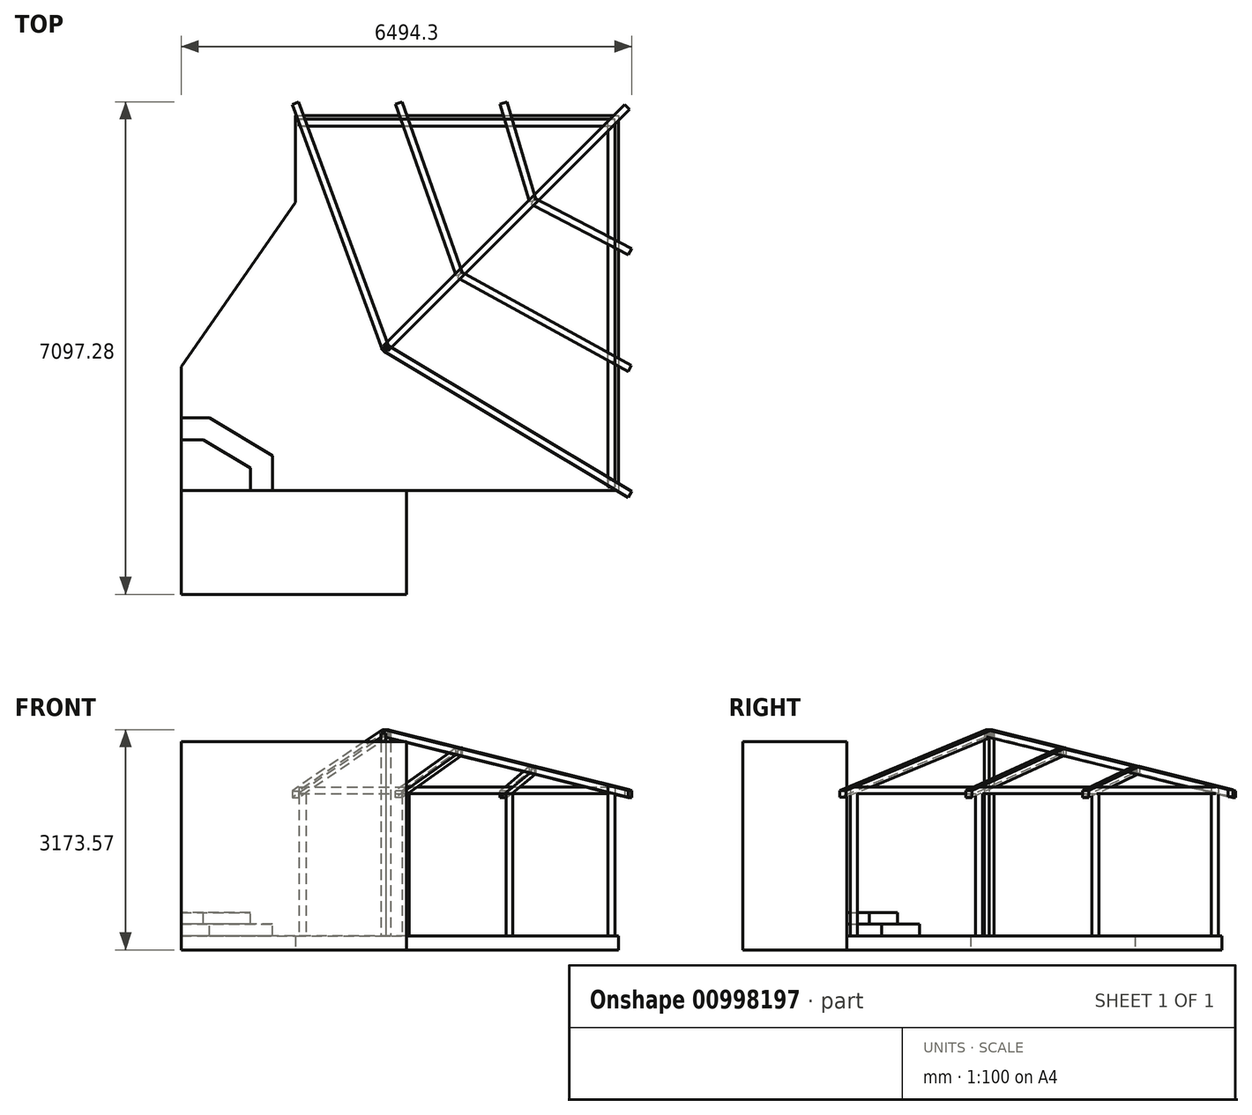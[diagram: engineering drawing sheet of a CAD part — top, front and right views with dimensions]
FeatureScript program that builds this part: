
annotation { "Feature Type Name" : "Feature", "Feature Type Description" : "" }
export const myFeature = defineFeature(function(context is Context, id is Id, definition is map)
    precondition{}
    {
        {
            var Q0;
            Q0=qCreatedBy(makeId("Top.planeOp"),FACE);
            var sketch = newSketch(context, id + "F0", { "sketchPlane" : qUnion([Q0])});
            skLineSegment(sketch, "E0", {"start": v(0, 0) * mm, "end": v(0, -5400) * mm});
            skLineSegment(sketch, "E1", {"start": v(0, -5400) * mm, "end": v(-6300, -5400) * mm});
            skLineSegment(sketch, "E2", {"start": v(-6300, -5400) * mm, "end": v(-6300, -3620) * mm});
            skLineSegment(sketch, "E3", {"start": v(-6300, -3620) * mm, "end": v(-4650, -1250) * mm});
            skLineSegment(sketch, "E4", {"start": v(-4650, -1250) * mm, "end": v(-4650, 0) * mm});
            skLineSegment(sketch, "E5", {"start": v(-4650, 0) * mm, "end": v(0, 0) * mm});
            skSolve(sketch);
        }
        {
            var Q0;
            Q0=makeQuery(id+"F0.imprint","IMPRINT",FACE,{"disambiguationData":[TD([[makeQuery(id+"F0.imprint","IMPRINT",EDGE,{"derivedFrom":sQuery(id+"F0.wireOp",EDGE,"E0")}),-1.0]])]});
            extrude(context, id + "F1", {"entities" : qUnion([Q0]), "depth" : 200 * mm, "offsetDistance" : 25 * mm});
        }
        {
            var Q0;
            Q0=makeQuery(id+"F1.opExtrude","CAP_FACE",FACE,{"disambiguationData":[OSD([sQuery(id+"F0.wireOp",EDGE,"E0"),sQuery(id+"F0.wireOp",EDGE,"E1"),sQuery(id+"F0.wireOp",EDGE,"E2"),sQuery(id+"F0.wireOp",EDGE,"E3"),sQuery(id+"F0.wireOp",EDGE,"E4"),sQuery(id+"F0.wireOp",EDGE,"E5")])],"isStart":false});
            var sketch = newSketch(context, id + "F2", { "sketchPlane" : qUnion([Q0])});
            skLineSegment(sketch, "E6.bottom", {"start": v(-50, -150) * mm, "end": v(-150, -150) * mm});
            skLineSegment(sketch, "E6.top", {"start": v(-50, -50) * mm, "end": v(-150, -50) * mm});
            skLineSegment(sketch, "E6.left", {"start": v(-50, -150) * mm, "end": v(-50, -50) * mm});
            skLineSegment(sketch, "E6.right", {"start": v(-150, -150) * mm, "end": v(-150, -50) * mm});
            skPoint(sketch, "E6.middle", {"position": v(-100, -100) * mm});
            skLineSegment(sketch, "E7", {"start": v(-100, -100) * mm, "end": v(-100, -5400) * mm, "construction": true});
            skLineSegment(sketch, "E8", {"start": v(-100, -100) * mm, "end": v(-4650, -100) * mm, "construction": true});
            skLineSegment(sketch, "E9.bottom", {"start": v(-150, -1870) * mm, "end": v(-50, -1870) * mm});
            skLineSegment(sketch, "E9.top", {"start": v(-150, -1770) * mm, "end": v(-50, -1770) * mm});
            skLineSegment(sketch, "E9.left", {"start": v(-150, -1870) * mm, "end": v(-150, -1770) * mm});
            skLineSegment(sketch, "E9.right", {"start": v(-50, -1870) * mm, "end": v(-50, -1770) * mm});
            skPoint(sketch, "E9.middle", {"position": v(-100, -1820) * mm});
            skLineSegment(sketch, "E10.bottom", {"start": v(-50, -3550) * mm, "end": v(-150, -3550) * mm});
            skLineSegment(sketch, "E10.top", {"start": v(-50, -3450) * mm, "end": v(-150, -3450) * mm});
            skLineSegment(sketch, "E10.left", {"start": v(-50, -3550) * mm, "end": v(-50, -3450) * mm});
            skLineSegment(sketch, "E10.right", {"start": v(-150, -3550) * mm, "end": v(-150, -3450) * mm});
            skPoint(sketch, "E10.middle", {"position": v(-100, -3500) * mm});
            skLineSegment(sketch, "E11.bottom", {"start": v(-1520, -150) * mm, "end": v(-1620, -150) * mm});
            skLineSegment(sketch, "E11.top", {"start": v(-1520, -50) * mm, "end": v(-1620, -50) * mm});
            skLineSegment(sketch, "E11.left", {"start": v(-1520, -150) * mm, "end": v(-1520, -50) * mm});
            skLineSegment(sketch, "E11.right", {"start": v(-1620, -150) * mm, "end": v(-1620, -50) * mm});
            skPoint(sketch, "E11.middle", {"position": v(-1570, -100) * mm});
            skPoint(sketch, "E12.middle", {"position": v(-3065, -100) * mm});
            skLineSegment(sketch, "E13.bottom", {"start": v(-4500, -150) * mm, "end": v(-4600, -150) * mm});
            skLineSegment(sketch, "E13.top", {"start": v(-4500, -50) * mm, "end": v(-4600, -50) * mm});
            skLineSegment(sketch, "E13.left", {"start": v(-4500, -150) * mm, "end": v(-4500, -50) * mm});
            skLineSegment(sketch, "E13.right", {"start": v(-4600, -150) * mm, "end": v(-4600, -50) * mm});
            skPoint(sketch, "E13.middle", {"position": v(-4550, -100) * mm});
            skLineSegment(sketch, "E14.bottom", {"start": v(-3015, -50) * mm, "end": v(-3115, -50) * mm});
            skLineSegment(sketch, "E14.top", {"start": v(-3015, -150) * mm, "end": v(-3115, -150) * mm});
            skLineSegment(sketch, "E14.left", {"start": v(-3015, -50) * mm, "end": v(-3015, -150) * mm});
            skLineSegment(sketch, "E14.right", {"start": v(-3115, -50) * mm, "end": v(-3115, -150) * mm});
            skSolve(sketch);
        }
        {
            var Q0;
            Q0 = qSketchRegion(id + "F2", true);
            extrude(context, id + "F3", {"entities" : qUnion([Q0]), "depth" : 2050 * mm, "offsetDistance" : 25 * mm});
        }
        {
            var Q0;
            Q0=makeQuery(id+"F3.opExtrude","CAP_FACE",FACE,{"disambiguationData":[OSD([sQuery(id+"F2.wireOp",EDGE,"E10.bottom"),sQuery(id+"F2.wireOp",EDGE,"E10.top"),sQuery(id+"F2.wireOp",EDGE,"E10.left"),sQuery(id+"F2.wireOp",EDGE,"E10.right")])],"isStart":false});
            var sketch = newSketch(context, id + "F4", { "sketchPlane" : qUnion([Q0])});
            skPoint(sketch, "E15.0", {"position": v(-4600, -50) * mm});
            skLineSegment(sketch, "E16.bottom", {"start": v(-4600, -50) * mm, "end": v(-50, -50) * mm});
            skLineSegment(sketch, "E16.top", {"start": v(-4600, -150) * mm, "end": v(-150, -150) * mm});
            skLineSegment(sketch, "E16.left", {"start": v(-4600, -50) * mm, "end": v(-4600, -150) * mm});
            skLineSegment(sketch, "E16.right", {"start": v(-50, -50) * mm, "end": v(-50, -150) * mm});
            skPoint(sketch, "E17.0", {"position": v(-150, -3550) * mm});
            skLineSegment(sketch, "E18.bottom", {"start": v(-50, -50) * mm, "end": v(-150, -50) * mm});
            skLineSegment(sketch, "E18.top", {"start": v(-50, -3550) * mm, "end": v(-150, -3550) * mm});
            skLineSegment(sketch, "E18.left", {"start": v(-50, -50) * mm, "end": v(-50, -3550) * mm});
            skLineSegment(sketch, "E18.right", {"start": v(-150, -150) * mm, "end": v(-150, -3550) * mm});
            skLineSegment(sketch, "E19", {"start": v(-150, -150) * mm, "end": v(-50, -50) * mm});
            skSolve(sketch);
        }
        {
            var Q0;
            Q0 = qSketchRegion(id + "F4", true);
            extrude(context, id + "F5", {"entities" : qUnion([Q0]), "depth" : 100 * mm, "offsetDistance" : 25 * mm});
        }
        {
            var Q0;
            Q0=qCreatedBy(makeId("Top.planeOp"),FACE);
            var sketch = newSketch(context, id + "F6", { "sketchPlane" : qUnion([Q0])});
            skPoint(sketch, "E20.0", {"position": v(-6300, -5400) * mm});
            skLineSegment(sketch, "E21.bottom", {"start": v(-6300, -5400) * mm, "end": v(-3050, -5400) * mm});
            skLineSegment(sketch, "E21.top", {"start": v(-6300, -6900) * mm, "end": v(-3050, -6900) * mm});
            skLineSegment(sketch, "E21.left", {"start": v(-6300, -5400) * mm, "end": v(-6300, -6900) * mm});
            skLineSegment(sketch, "E21.right", {"start": v(-3050, -5400) * mm, "end": v(-3050, -6900) * mm});
            skSolve(sketch);
        }
        {
            var Q0;
            Q0=makeQuery(id+"F5.opExtrude","SWEPT_FACE",FACE,{"disambiguationData":[OSD([sQuery(id+"F4.wireOp",EDGE,"E18.right")])]});
            var Q1;
            Q1=makeQuery(id+"F5.opExtrude","SWEPT_FACE",FACE,{"disambiguationData":[OSD([sQuery(id+"F4.wireOp",EDGE,"E16.top")])]});
            cPlane(context, id + "F7", {"entities" : qUnion([Q0, Q1]), "cplaneType" : CPlaneType.MID_PLANE, "offset" : 25 * mm, "width" : 150 * mm, "height" : 150 * mm});
        }
        {
            var Q0;
            Q0=makeQuery(id+"F1.opExtrude","CAP_FACE",FACE,{"disambiguationData":[OSD([sQuery(id+"F0.wireOp",EDGE,"E0"),sQuery(id+"F0.wireOp",EDGE,"E1"),sQuery(id+"F0.wireOp",EDGE,"E2"),sQuery(id+"F0.wireOp",EDGE,"E3"),sQuery(id+"F0.wireOp",EDGE,"E4"),sQuery(id+"F0.wireOp",EDGE,"E5")])],"isStart":false});
            var sketch = newSketch(context, id + "F8", { "sketchPlane" : qUnion([Q0])});
            skLineSegment(sketch, "E22.0", {"start": v(-100, -100) * mm, "end": v(-100, -5400) * mm, "construction": true});
            skLineSegment(sketch, "E23.bottom", {"start": v(-150, -5250) * mm, "end": v(-50, -5250) * mm});
            skLineSegment(sketch, "E23.top", {"start": v(-150, -5350) * mm, "end": v(-50, -5350) * mm});
            skLineSegment(sketch, "E23.left", {"start": v(-150, -5250) * mm, "end": v(-150, -5350) * mm});
            skLineSegment(sketch, "E23.right", {"start": v(-50, -5250) * mm, "end": v(-50, -5350) * mm});
            skPoint(sketch, "E23.middle", {"position": v(-100, -5300) * mm});
            skSolve(sketch);
        }
        {
            var Q0;
            Q0 = qSketchRegion(id + "F8", true);
            extrude(context, id + "F9", {"entities" : qUnion([Q0]), "operationType" : NewBodyOperationType.ADD, "depth" : 2050 * mm, "offsetDistance" : 25 * mm});
        }
        {
            var Q0;
            Q0=makeQuery(id+"F5.opExtrude","SWEPT_FACE",FACE,{"disambiguationData":[OSD([sQuery(id+"F4.wireOp",EDGE,"E18.top")])]});
            var Q1;
            Q1=makeQuery(id+"F9.opExtrude","SWEPT_FACE",FACE,{"disambiguationData":[OSD([sQuery(id+"F8.wireOp",EDGE,"E23.top")])]});
            extrude(context, id + "F10", {"entities" : qUnion([Q0]), "operationType" : NewBodyOperationType.ADD, "endBound" : BoundingType.UP_TO_SURFACE, "depth" : 25 * mm, "endBoundEntityFace" : qUnion([Q1]), "offsetDistance" : 25 * mm});
        }
        {
            var Q0;
            Q0=makeQuery(id+"F8.imprint","IMPRINT",FACE,{"disambiguationData":[TD([[makeQuery(id+"F8.imprint","IMPRINT",EDGE,{"derivedFrom":sQuery(id+"F8.wireOp",EDGE,"E23.bottom")}),1.0]])]});
            var sketch = newSketch(context, id + "F11", { "sketchPlane" : qUnion([Q0])});
            skPoint(sketch, "E24.0", {"position": v(-100, -100) * mm});
            skPoint(sketch, "E25.0", {"position": v(-4550, -100) * mm});
            skPoint(sketch, "E26.0", {"position": v(-100, -5300) * mm});
            skLineSegment(sketch, "E27", {"start": v(-100, -100) * mm, "end": v(-1231.37, -1231.37) * mm, "construction": true});
            skLineSegment(sketch, "E28", {"start": v(-3352.7, -3352.7) * mm, "end": v(-4550, -100) * mm, "construction": true});
            skLineSegment(sketch, "E29", {"start": v(-3352.7, -3352.7) * mm, "end": v(-100, -5300) * mm, "construction": true});
            skPoint(sketch, "E30.0", {"position": v(-100, -1820) * mm});
            skPoint(sketch, "E31.0", {"position": v(-100, -3500) * mm});
            skPoint(sketch, "E32.0", {"position": v(-1570, -100) * mm});
            skPoint(sketch, "E33.0", {"position": v(-3065, -100) * mm});
            skLineSegment(sketch, "E34", {"start": v(-100, -1820) * mm, "end": v(-1231.37, -1231.37) * mm, "construction": true});
            skLineSegment(sketch, "E35", {"start": v(-100, -3500) * mm, "end": v(-2292.03, -2292.03) * mm, "construction": true});
            skLineSegment(sketch, "E36", {"start": v(-1231.37, -1231.37) * mm, "end": v(-1231.37, -1231.37) * mm});
            skLineSegment(sketch, "E37", {"start": v(-2292.03, -2292.03) * mm, "end": v(-3065, -100) * mm, "construction": true});
            skLineSegment(sketch, "E38", {"start": v(-2292.03, -2292.03) * mm, "end": v(-3352.7, -3352.7) * mm, "construction": true});
            skLineSegment(sketch, "E39", {"start": v(-1231.37, -1231.37) * mm, "end": v(-1570, -100) * mm, "construction": true});
            skLineSegment(sketch, "E40", {"start": v(-1231.37, -1231.37) * mm, "end": v(-2292.03, -2292.03) * mm, "construction": true});
            skSolve(sketch);
        }
        {
            var Q0;
            Q0=qCreatedBy(id+"F7.planeOp",FACE);
            var sketch = newSketch(context, id + "F12", { "sketchPlane" : qUnion([Q0])});
            skLineSegment(sketch, "E41", {"start": v(4741.42, 3123.57) * mm, "end": v(-175.5, 2256.59) * mm});
            skPoint(sketch, "E42.0", {"position": v(3818.38, 200) * mm});
            skPoint(sketch, "E43.0", {"position": v(3288.05, 200) * mm});
            skPoint(sketch, "E44.0", {"position": v(4741.42, 200) * mm});
            skLineSegment(sketch, "E45", {"start": v(4741.42, 3123.57) * mm, "end": v(4741.42, 200) * mm, "construction": true});
            skPoint(sketch, "E46.0", {"position": v(3241.42, 200) * mm});
            skPoint(sketch, "E47.0", {"position": v(1741.42, 200) * mm});
            skLineSegment(sketch, "E48", {"start": v(3241.42, 200) * mm, "end": v(3241.42, 2859.08) * mm, "construction": true});
            skLineSegment(sketch, "E49", {"start": v(1741.42, 200) * mm, "end": v(1741.42, 2594.6) * mm, "construction": true});
            skSolve(sketch);
        }
        {
            var Q0;
            Q0=sQuery(id+"F12.wireOp",EDGE,"E45");
            var Q1;
            Q1=qCreatedBy(id+"F7.planeOp",FACE);
            cPlane(context, id + "F13", {"entities" : qUnion([Q0, Q1]), "cplaneType" : CPlaneType.LINE_ANGLE, "offset" : 25 * mm, "angle" : 90 * degree, "width" : 150 * mm, "height" : 150 * mm});
        }
        {
            var Q0;
            Q0=qCreatedBy(id+"F13.planeOp",FACE);
            var sketch = newSketch(context, id + "F14", { "sketchPlane" : qUnion([Q0])});
            skPoint(sketch, "E50.0", {"position": v(0, 3123.57) * mm});
            skLineSegment(sketch, "E51.bottom", {"start": v(-50, 3173.57) * mm, "end": v(50, 3173.57) * mm});
            skLineSegment(sketch, "E51.top", {"start": v(-50, 3073.57) * mm, "end": v(50, 3073.57) * mm});
            skLineSegment(sketch, "E51.left", {"start": v(-50, 3173.57) * mm, "end": v(-50, 3073.57) * mm});
            skLineSegment(sketch, "E51.right", {"start": v(50, 3173.57) * mm, "end": v(50, 3073.57) * mm});
            skSolve(sketch);
        }
        {
            var Q0;
            Q0=makeQuery(id+"F14.imprint","IMPRINT",FACE,{"disambiguationData":[TD([[makeQuery(id+"F14.imprint","IMPRINT",EDGE,{"derivedFrom":sQuery(id+"F14.wireOp",EDGE,"E51.bottom")}),-1.0]])]});
            var Q1;
            Q1=sQuery(id+"F12.wireOp",EDGE,"E41");
            sweep(context, id + "F15", {"profiles" : qUnion([Q0]), "path" : qUnion([Q1])});
        }
        {
            var Q0;
            Q0=sQuery(id+"F12.wireOp",EDGE,"E45");
            var Q1;
            Q1=sQuery(id+"F11.wireOp",EDGE,"E29");
            cPlane(context, id + "F16", {"entities" : qUnion([Q0, Q1]), "cplaneType" : CPlaneType.LINE_ANGLE, "offset" : 25 * mm, "angle" : 0 * degree, "width" : 150 * mm, "height" : 150 * mm});
        }
        {
            var Q0;
            Q0=qCreatedBy(id+"F16.planeOp",FACE);
            var sketch = newSketch(context, id + "F17", { "sketchPlane" : qUnion([Q0])});
            skPoint(sketch, "E52.0", {"position": v(2636.6, 200) * mm});
            skPoint(sketch, "E53.0", {"position": v(2662.28, 2250) * mm});
            skLineSegment(sketch, "E54", {"start": v(2636.6, 200) * mm, "end": v(2636.6, 2250) * mm, "construction": true});
            skPoint(sketch, "E55.0", {"position": v(-1154.44, 3123.57) * mm});
            skPoint(sketch, "E56.0", {"position": v(2705.18, 2300) * mm});
            skLineSegment(sketch, "E57", {"start": v(-1154.44, 3123.57) * mm, "end": v(2949.68, 2247.83) * mm});
            skSolve(sketch);
        }
        {
            var Q0;
            Q0=sQuery(id+"F12.wireOp",EDGE,"E45");
            var Q1;
            Q1=qCreatedBy(id+"F16.planeOp",FACE);
            cPlane(context, id + "F18", {"entities" : qUnion([Q0, Q1]), "cplaneType" : CPlaneType.LINE_ANGLE, "offset" : 25 * mm, "angle" : 90 * degree, "width" : 150 * mm, "height" : 150 * mm});
        }
        {
            var Q0;
            Q0=qCreatedBy(id+"F18.planeOp",FACE);
            var sketch = newSketch(context, id + "F19", { "sketchPlane" : qUnion([Q0])});
            skPoint(sketch, "E58.0", {"position": v(-4598.73, 3123.57) * mm});
            skLineSegment(sketch, "E59.bottom", {"start": v(-4648.73, 3173.57) * mm, "end": v(-4548.73, 3173.57) * mm});
            skLineSegment(sketch, "E59.top", {"start": v(-4648.73, 3073.57) * mm, "end": v(-4548.73, 3073.57) * mm});
            skLineSegment(sketch, "E59.left", {"start": v(-4648.73, 3173.57) * mm, "end": v(-4648.73, 3073.57) * mm});
            skLineSegment(sketch, "E59.right", {"start": v(-4548.73, 3173.57) * mm, "end": v(-4548.73, 3073.57) * mm});
            skSolve(sketch);
        }
        {
            var Q0;
            Q0 = qSketchRegion(id + "F19", true);
            var Q1;
            Q1=sQuery(id+"F17.wireOp",EDGE,"E57");
            sweep(context, id + "F20", {"profiles" : qUnion([Q0]), "path" : qUnion([Q1])});
        }
        {
            var Q0;
            Q0=sQuery(id+"F12.wireOp",EDGE,"E48");
            var Q1;
            Q1=sQuery(id+"F11.wireOp",EDGE,"E35");
            cPlane(context, id + "F21", {"entities" : qUnion([Q0, Q1]), "cplaneType" : CPlaneType.LINE_ANGLE, "offset" : 25 * mm, "angle" : 0 * degree, "width" : 150 * mm, "height" : 150 * mm});
        }
        {
            var Q0;
            Q0=qCreatedBy(id+"F21.planeOp",FACE);
            var sketch = newSketch(context, id + "F22", { "sketchPlane" : qUnion([Q0])});
            skPoint(sketch, "E60.0", {"position": v(-901.18, 2859.08) * mm});
            skLineSegment(sketch, "E61", {"start": v(1658.75, 2350) * mm, "end": v(1658.75, 2250) * mm, "construction": true});
            skPoint(sketch, "E62", {"position": v(1658.75, 2300) * mm});
            skLineSegment(sketch, "E63", {"start": v(-901.18, 2859.08) * mm, "end": v(1903, 2246.66) * mm});
            skSolve(sketch);
        }
        {
            var Q0;
            Q0=sQuery(id+"F12.wireOp",EDGE,"E48");
            var Q1;
            Q1=qCreatedBy(id+"F21.planeOp",FACE);
            cPlane(context, id + "F23", {"entities" : qUnion([Q0, Q1]), "cplaneType" : CPlaneType.LINE_ANGLE, "offset" : 25 * mm, "angle" : 90 * degree, "width" : 150 * mm, "height" : 150 * mm});
        }
        {
            var Q0;
            Q0=qCreatedBy(id+"F23.planeOp",FACE);
            var sketch = newSketch(context, id + "F24", { "sketchPlane" : qUnion([Q0])});
            skPoint(sketch, "E64.0", {"position": v(3113.63, 2859.08) * mm});
            skLineSegment(sketch, "E65.bottom", {"start": v(3063.63, 2909.08) * mm, "end": v(3163.63, 2909.08) * mm});
            skLineSegment(sketch, "E65.top", {"start": v(3063.63, 2809.08) * mm, "end": v(3163.63, 2809.08) * mm});
            skLineSegment(sketch, "E65.left", {"start": v(3063.63, 2909.08) * mm, "end": v(3063.63, 2809.08) * mm});
            skLineSegment(sketch, "E65.right", {"start": v(3163.63, 2909.08) * mm, "end": v(3163.63, 2809.08) * mm});
            skSolve(sketch);
        }
        {
            var Q0;
            Q0 = qSketchRegion(id + "F24", true);
            var Q1;
            Q1=sQuery(id+"F22.wireOp",EDGE,"E63");
            sweep(context, id + "F25", {"profiles" : qUnion([Q0]), "path" : qUnion([Q1])});
        }
        {
            var Q0;
            Q0=sQuery(id+"F12.wireOp",EDGE,"E49");
            var Q1;
            Q1=sQuery(id+"F11.wireOp",EDGE,"E34");
            cPlane(context, id + "F26", {"entities" : qUnion([Q0, Q1]), "cplaneType" : CPlaneType.LINE_ANGLE, "offset" : 25 * mm, "angle" : 0 * degree, "width" : 150 * mm, "height" : 150 * mm});
        }
        {
            var Q0;
            Q0=qCreatedBy(id+"F26.planeOp",FACE);
            var sketch = newSketch(context, id + "F27", { "sketchPlane" : qUnion([Q0])});
            skPoint(sketch, "E66.0", {"position": v(-524.03, 2594.6) * mm});
            skLineSegment(sketch, "E67", {"start": v(807.67, 2350) * mm, "end": v(807.67, 2250) * mm, "construction": true});
            skPoint(sketch, "E68", {"position": v(807.67, 2300) * mm});
            skLineSegment(sketch, "E69", {"start": v(-524.03, 2594.6) * mm, "end": v(1051.77, 2246) * mm});
            skSolve(sketch);
        }
        {
            var Q0;
            Q0=qCreatedBy(id+"F26.planeOp",FACE);
            var Q1;
            Q1=sQuery(id+"F12.wireOp",EDGE,"E49");
            cPlane(context, id + "F28", {"entities" : qUnion([Q0, Q1]), "cplaneType" : CPlaneType.LINE_ANGLE, "offset" : 25 * mm, "angle" : 90 * degree, "width" : 150 * mm, "height" : 150 * mm});
        }
        {
            var Q0;
            Q0=qCreatedBy(id+"F28.planeOp",FACE);
            var sketch = newSketch(context, id + "F29", { "sketchPlane" : qUnion([Q0])});
            skPoint(sketch, "E70.0", {"position": v(1660.7, 2594.6) * mm});
            skLineSegment(sketch, "E71.bottom", {"start": v(1610.7, 2644.6) * mm, "end": v(1710.7, 2644.6) * mm});
            skLineSegment(sketch, "E71.top", {"start": v(1610.7, 2544.6) * mm, "end": v(1710.7, 2544.6) * mm});
            skLineSegment(sketch, "E71.left", {"start": v(1610.7, 2644.6) * mm, "end": v(1610.7, 2544.6) * mm});
            skLineSegment(sketch, "E71.right", {"start": v(1710.7, 2644.6) * mm, "end": v(1710.7, 2544.6) * mm});
            skSolve(sketch);
        }
        {
            var Q0;
            Q0 = qSketchRegion(id + "F29", true);
            var Q1;
            Q1=sQuery(id+"F27.wireOp",EDGE,"E69");
            sweep(context, id + "F30", {"profiles" : qUnion([Q0]), "path" : qUnion([Q1])});
        }
        {
            var Q0;
            Q0=sQuery(id+"F11.wireOp",EDGE,"E39");
            var Q1;
            Q1=sQuery(id+"F12.wireOp",EDGE,"E49");
            cPlane(context, id + "F31", {"entities" : qUnion([Q0, Q1]), "cplaneType" : CPlaneType.LINE_ANGLE, "offset" : 25 * mm, "angle" : 0 * degree, "width" : 150 * mm, "height" : 150 * mm});
        }
        {
            var Q0;
            Q0=qCreatedBy(id+"F31.planeOp",FACE);
            var sketch = newSketch(context, id + "F32", { "sketchPlane" : qUnion([Q0])});
            skPoint(sketch, "E72.0", {"position": v(-826.58, 2594.6) * mm});
            skLineSegment(sketch, "E73", {"start": v(406.57, 2350) * mm, "end": v(406.57, 2250) * mm, "construction": true});
            skPoint(sketch, "E74", {"position": v(406.57, 2300) * mm});
            skLineSegment(sketch, "E75", {"start": v(-826.58, 2594.6) * mm, "end": v(649.73, 2241.91) * mm});
            skSolve(sketch);
        }
        {
            var Q0;
            Q0=qCreatedBy(id+"F31.planeOp",FACE);
            var Q1;
            Q1=sQuery(id+"F12.wireOp",EDGE,"E49");
            cPlane(context, id + "F33", {"entities" : qUnion([Q0, Q1]), "cplaneType" : CPlaneType.LINE_ANGLE, "offset" : 25 * mm, "angle" : 90 * degree, "width" : 150 * mm, "height" : 150 * mm});
        }
        {
            var Q0;
            Q0=qCreatedBy(id+"F33.planeOp",FACE);
            var sketch = newSketch(context, id + "F34", { "sketchPlane" : qUnion([Q0])});
            skPoint(sketch, "E76.0", {"position": v(-1532.75, 2594.6) * mm});
            skLineSegment(sketch, "E77.bottom", {"start": v(-1482.75, 2544.6) * mm, "end": v(-1582.75, 2544.6) * mm});
            skLineSegment(sketch, "E77.top", {"start": v(-1482.75, 2644.6) * mm, "end": v(-1582.75, 2644.6) * mm});
            skLineSegment(sketch, "E77.left", {"start": v(-1482.75, 2544.6) * mm, "end": v(-1482.75, 2644.6) * mm});
            skLineSegment(sketch, "E77.right", {"start": v(-1582.75, 2544.6) * mm, "end": v(-1582.75, 2644.6) * mm});
            skSolve(sketch);
        }
        {
            var Q0;
            Q0 = qSketchRegion(id + "F34", true);
            var Q1;
            Q1=sQuery(id+"F32.wireOp",EDGE,"E75");
            sweep(context, id + "F35", {"profiles" : qUnion([Q0]), "path" : qUnion([Q1])});
        }
        {
            var Q0;
            Q0=sQuery(id+"F12.wireOp",EDGE,"E48");
            var Q1;
            Q1=sQuery(id+"F11.wireOp",EDGE,"E37");
            cPlane(context, id + "F36", {"entities" : qUnion([Q0, Q1]), "cplaneType" : CPlaneType.LINE_ANGLE, "offset" : 25 * mm, "angle" : 0 * degree, "width" : 150 * mm, "height" : 150 * mm});
        }
        {
            var Q0;
            Q0=qCreatedBy(id+"F36.planeOp",FACE);
            var sketch = newSketch(context, id + "F37", { "sketchPlane" : qUnion([Q0])});
            skPoint(sketch, "E78.0", {"position": v(1399.35, 2859.08) * mm});
            skLineSegment(sketch, "E79", {"start": v(-978, 2250) * mm, "end": v(-978, 2350) * mm, "construction": true});
            skPoint(sketch, "E80", {"position": v(-978, 2300) * mm});
            skLineSegment(sketch, "E81", {"start": v(1399.35, 2859.08) * mm, "end": v(-1221.36, 2242.77) * mm});
            skSolve(sketch);
        }
        {
            var Q0;
            Q0=qCreatedBy(id+"F36.planeOp",FACE);
            var Q1;
            Q1=sQuery(id+"F12.wireOp",EDGE,"E48");
            cPlane(context, id + "F38", {"entities" : qUnion([Q0, Q1]), "cplaneType" : CPlaneType.LINE_ANGLE, "offset" : 25 * mm, "angle" : 90 * degree, "width" : 150 * mm, "height" : 150 * mm});
        }
        {
            var Q0;
            Q0=qCreatedBy(id+"F38.planeOp",FACE);
            var sketch = newSketch(context, id + "F39", { "sketchPlane" : qUnion([Q0])});
            skPoint(sketch, "E82.0", {"position": v(2923.8, 2859.08) * mm});
            skLineSegment(sketch, "E83.bottom", {"start": v(2873.8, 2809.08) * mm, "end": v(2973.8, 2809.08) * mm});
            skLineSegment(sketch, "E83.top", {"start": v(2873.8, 2909.08) * mm, "end": v(2973.8, 2909.08) * mm});
            skLineSegment(sketch, "E83.left", {"start": v(2873.8, 2809.08) * mm, "end": v(2873.8, 2909.08) * mm});
            skLineSegment(sketch, "E83.right", {"start": v(2973.8, 2809.08) * mm, "end": v(2973.8, 2909.08) * mm});
            skSolve(sketch);
        }
        {
            var Q0;
            Q0 = qSketchRegion(id + "F39", true);
            var Q1;
            Q1=sQuery(id+"F37.wireOp",EDGE,"E81");
            sweep(context, id + "F40", {"profiles" : qUnion([Q0]), "path" : qUnion([Q1])});
        }
        {
            var Q0;
            Q0=sQuery(id+"F12.wireOp",EDGE,"E45");
            var Q1;
            Q1=sQuery(id+"F11.wireOp",EDGE,"E28");
            cPlane(context, id + "F41", {"entities" : qUnion([Q0, Q1]), "cplaneType" : CPlaneType.LINE_ANGLE, "offset" : 25 * mm, "angle" : 0 * degree, "width" : 150 * mm, "height" : 150 * mm});
        }
        {
            var Q0;
            Q0=qCreatedBy(id+"F41.planeOp",FACE);
            var sketch = newSketch(context, id + "F42", { "sketchPlane" : qUnion([Q0])});
            skPoint(sketch, "E84.0", {"position": v(-1988.16, 3123.57) * mm});
            skLineSegment(sketch, "E85", {"start": v(1531.18, 2350) * mm, "end": v(1531.18, 2250) * mm, "construction": true});
            skPoint(sketch, "E86", {"position": v(1531.18, 2300) * mm});
            skLineSegment(sketch, "E87", {"start": v(-1988.16, 3123.57) * mm, "end": v(1774.6, 2243.04) * mm});
            skSolve(sketch);
        }
        {
            var Q0;
            Q0=qCreatedBy(id+"F41.planeOp",FACE);
            var Q1;
            Q1=sQuery(id+"F12.wireOp",EDGE,"E45");
            cPlane(context, id + "F43", {"entities" : qUnion([Q0, Q1]), "cplaneType" : CPlaneType.LINE_ANGLE, "offset" : 25 * mm, "angle" : 90 * degree, "width" : 150 * mm, "height" : 150 * mm});
        }
        {
            var Q0;
            Q0=qCreatedBy(id+"F43.planeOp",FACE);
            var sketch = newSketch(context, id + "F44", { "sketchPlane" : qUnion([Q0])});
            skPoint(sketch, "E88.0", {"position": v(4304.45, 3123.57) * mm});
            skLineSegment(sketch, "E89.bottom", {"start": v(4354.45, 3173.57) * mm, "end": v(4254.45, 3173.57) * mm});
            skLineSegment(sketch, "E89.top", {"start": v(4354.45, 3073.57) * mm, "end": v(4254.45, 3073.57) * mm});
            skLineSegment(sketch, "E89.left", {"start": v(4354.45, 3173.57) * mm, "end": v(4354.45, 3073.57) * mm});
            skLineSegment(sketch, "E89.right", {"start": v(4254.45, 3173.57) * mm, "end": v(4254.45, 3073.57) * mm});
            skSolve(sketch);
        }
        {
            var Q0;
            Q0 = qSketchRegion(id + "F44", true);
            var Q1;
            Q1=sQuery(id+"F42.wireOp",EDGE,"E87");
            sweep(context, id + "F45", {"profiles" : qUnion([Q0]), "path" : qUnion([Q1])});
        }
        {
            var Q0;
            Q0=makeQuery(id+"F8.imprint","IMPRINT",FACE,{"disambiguationData":[TD([[makeQuery(id+"F8.imprint","IMPRINT",EDGE,{"derivedFrom":sQuery(id+"F8.wireOp",EDGE,"E23.bottom")}),1.0]])]});
            var sketch = newSketch(context, id + "F46", { "sketchPlane" : qUnion([Q0])});
            skPoint(sketch, "E90.0", {"position": v(-3352.7, -3352.7) * mm});
            skLineSegment(sketch, "E91.0", {"start": v(-3388.05, -3317.34) * mm, "end": v(-3317.34, -3388.05) * mm});
            skLineSegment(sketch, "E92", {"start": v(-3352.7, -3281.98) * mm, "end": v(-3423.4, -3352.7) * mm});
            skLineSegment(sketch, "E93", {"start": v(-3423.4, -3352.7) * mm, "end": v(-3352.7, -3423.4) * mm});
            skLineSegment(sketch, "E94", {"start": v(-3352.7, -3423.4) * mm, "end": v(-3281.98, -3352.7) * mm});
            skLineSegment(sketch, "E95", {"start": v(-3281.98, -3352.7) * mm, "end": v(-3352.7, -3281.98) * mm});
            skLineSegment(sketch, "E96", {"start": v(-3352.7, -3281.98) * mm, "end": v(-3352.7, -3423.4) * mm, "construction": true});
            skSolve(sketch);
        }
        {
            var Q0;
            Q0 = qSketchRegion(id + "F46", true);
            var Q1;
            Q1=sQuery(id+"F12.wireOp",VERTEX,"E41.start");
            extrude(context, id + "F47", {"entities" : qUnion([Q0]), "endBound" : BoundingType.UP_TO_VERTEX, "depth" : 25 * mm, "endBoundEntityVertex" : qUnion([Q1]), "offsetDistance" : 25 * mm});
        }
        {
            var Q0;
            Q0=makeQuery(id+"F6.imprint","IMPRINT",FACE,{"disambiguationData":[TD([[makeQuery(id+"F6.imprint","IMPRINT",EDGE,{"derivedFrom":sQuery(id+"F6.wireOp",EDGE,"E21.bottom")}),-1.0]])]});
            extrude(context, id + "F48", {"entities" : qUnion([Q0]), "depth" : 3000 * mm, "offsetDistance" : 25 * mm});
        }
        {
            var Q0;
            Q0=makeQuery(id+"F8.imprint","IMPRINT",FACE,{"disambiguationData":[TD([[makeQuery(id+"F8.imprint","IMPRINT",EDGE,{"derivedFrom":sQuery(id+"F8.wireOp",EDGE,"E23.bottom")}),1.0]])]});
            cPlane(context, id + "F49", {"entities" : qUnion([Q0]), "cplaneType" : CPlaneType.OFFSET, "offset" : 340 * mm, "width" : 150 * mm, "height" : 150 * mm});
        }
        {
            var Q0;
            Q0=qCreatedBy(id+"F49.planeOp",FACE);
            var sketch = newSketch(context, id + "F50", { "sketchPlane" : qUnion([Q0])});
            skPoint(sketch, "E97.0", {"position": v(-6300, -5400) * mm});
            skLineSegment(sketch, "E98", {"start": v(-6300, -5400) * mm, "end": v(-5300, -5400) * mm});
            skLineSegment(sketch, "E99", {"start": v(-5300, -5400) * mm, "end": v(-5300, -5080) * mm});
            skLineSegment(sketch, "E100", {"start": v(-5300, -5080) * mm, "end": v(-5980, -4672.9) * mm});
            skLineSegment(sketch, "E101", {"start": v(-5980, -4672.9) * mm, "end": v(-6300, -4672.9) * mm});
            skLineSegment(sketch, "E102", {"start": v(-6300, -4672.9) * mm, "end": v(-6300, -5400) * mm});
            skSolve(sketch);
        }
        {
            var Q0;
            Q0=makeQuery(id+"F50.imprint","IMPRINT",FACE,{"disambiguationData":[TD([[makeQuery(id+"F50.imprint","IMPRINT",EDGE,{"derivedFrom":sQuery(id+"F50.wireOp",EDGE,"E98")}),1.0]])]});
            extrude(context, id + "F51", {"entities" : qUnion([Q0]), "oppositeDirection" : true, "depth" : 170 * mm, "offsetDistance" : 25 * mm});
        }
        {
            var Q0;
            Q0=makeQuery(id+"F51.opExtrude","CAP_FACE",FACE,{"disambiguationData":[OSD([sQuery(id+"F50.wireOp",EDGE,"E98"),sQuery(id+"F50.wireOp",EDGE,"E99"),sQuery(id+"F50.wireOp",EDGE,"E100"),sQuery(id+"F50.wireOp",EDGE,"E101"),sQuery(id+"F50.wireOp",EDGE,"E102")])],"isStart":false});
            var sketch = newSketch(context, id + "F52", { "sketchPlane" : qUnion([Q0])});
            skLineSegment(sketch, "E103.0", {"start": v(-6300, 5400) * mm, "end": v(-6300, 4352.9) * mm});
            skLineSegment(sketch, "E104.0", {"start": v(-4980, 5400) * mm, "end": v(-6300, 5400) * mm});
            skLineSegment(sketch, "E105.0", {"start": v(-5891.53, 4352.9) * mm, "end": v(-6300, 4352.9) * mm});
            skLineSegment(sketch, "E105.1", {"start": v(-4980, 4898.61) * mm, "end": v(-5891.53, 4352.9) * mm});
            skLineSegment(sketch, "E105.2", {"start": v(-4980, 5400) * mm, "end": v(-4980, 4898.61) * mm});
            skPoint(sketch, "E106.orphan", {"position": v(0, 5400) * mm});
            skPoint(sketch, "E107.orphan", {"position": v(-6300, 3620) * mm});
            skSolve(sketch);
        }
        {
            var Q0;
            Q0 = qSketchRegion(id + "F52", true);
            var Q1;
            Q1=makeQuery(id+"F1.opExtrude","CAP_FACE",FACE,{"disambiguationData":[OSD([sQuery(id+"F0.wireOp",EDGE,"E0"),sQuery(id+"F0.wireOp",EDGE,"E1"),sQuery(id+"F0.wireOp",EDGE,"E2"),sQuery(id+"F0.wireOp",EDGE,"E3"),sQuery(id+"F0.wireOp",EDGE,"E4"),sQuery(id+"F0.wireOp",EDGE,"E5")])],"isStart":false});
            extrude(context, id + "F53", {"entities" : qUnion([Q0]), "endBound" : BoundingType.UP_TO_SURFACE, "depth" : 25 * mm, "endBoundEntityFace" : qUnion([Q1]), "offsetDistance" : 25 * mm});
        }
    });
